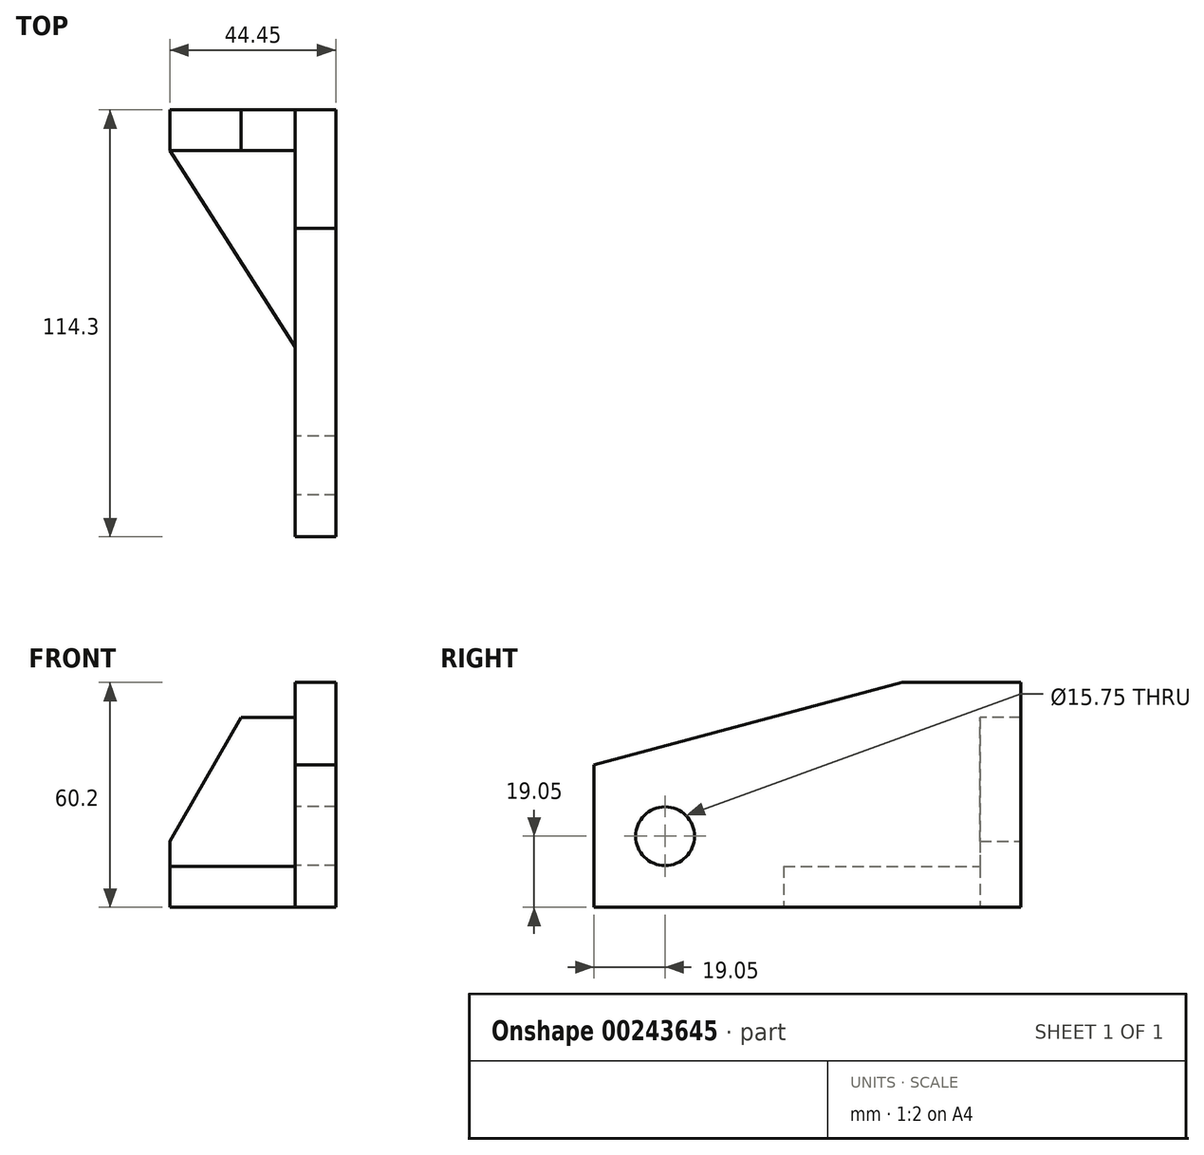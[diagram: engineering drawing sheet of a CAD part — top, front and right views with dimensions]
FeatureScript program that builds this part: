
annotation { "Feature Type Name" : "Feature", "Feature Type Description" : "" }
export const myFeature = defineFeature(function(context is Context, id is Id, definition is map)
    precondition{}
    {
        {
            var Q0;
            Q0=qCreatedBy(makeId("Top.planeOp"),FACE);
            var sketch = newSketch(context, id + "F0", { "sketchPlane" : qUnion([Q0])});
            skLineSegment(sketch, "E0", {"start": v(-20.72, 21.7) * mm, "end": v(12.81, 21.7) * mm});
            skLineSegment(sketch, "E1", {"start": v(12.81, -30.88) * mm, "end": v(12.81, 21.7) * mm});
            skLineSegment(sketch, "E2", {"start": v(-20.72, 21.7) * mm, "end": v(12.81, -30.88) * mm});
            skLineSegment(sketch, "E3", {"start": v(-20.72, 21.7) * mm, "end": v(-20.72, 32.62) * mm});
            skLineSegment(sketch, "E4", {"start": v(-20.72, 32.62) * mm, "end": v(12.81, 32.62) * mm});
            skLineSegment(sketch, "E5", {"start": v(12.81, 32.62) * mm, "end": v(12.81, 21.7) * mm});
            skLineSegment(sketch, "E6", {"start": v(12.81, 32.62) * mm, "end": v(23.73, 32.62) * mm});
            skLineSegment(sketch, "E7", {"start": v(23.73, 32.62) * mm, "end": v(23.73, -81.68) * mm});
            skLineSegment(sketch, "E8", {"start": v(23.73, -81.68) * mm, "end": v(12.81, -81.68) * mm});
            skLineSegment(sketch, "E9", {"start": v(12.81, -81.68) * mm, "end": v(12.81, -30.88) * mm});
            skSolve(sketch);
        }
        {
            var Q0;
            Q0=makeQuery(id+"F0.imprint","IMPRINT",FACE,{"disambiguationData":[TD([[makeQuery(id+"F0.imprint","IMPRINT",EDGE,{"derivedFrom":sQuery(id+"F0.wireOp",EDGE,"E0")}),-1.0]])]});
            extrude(context, id + "F1", {"entities" : qUnion([Q0]), "depth" : 10.92 * mm});
        }
        {
            var Q0;
            Q0=makeQuery(id+"F0.imprint","IMPRINT",FACE,{"disambiguationData":[TD([[makeQuery(id+"F0.imprint","IMPRINT",EDGE,{"derivedFrom":sQuery(id+"F0.wireOp",EDGE,"E1")}),-1.0]])]});
            extrude(context, id + "F2", {"entities" : qUnion([Q0]), "operationType" : NewBodyOperationType.ADD, "depth" : 60.2 * mm});
        }
        {
            var Q0;
            Q0=makeQuery(id+"F0.imprint","IMPRINT",FACE,{"disambiguationData":[TD([[makeQuery(id+"F0.imprint","IMPRINT",EDGE,{"derivedFrom":sQuery(id+"F0.wireOp",EDGE,"E0")}),1.0]])]});
            extrude(context, id + "F3", {"entities" : qUnion([Q0]), "operationType" : NewBodyOperationType.ADD, "depth" : 50.8 * mm});
        }
        {
            var Q0;
            Q0=makeQuery(id+"F3.opExtrude","CAP_EDGE",EDGE,{"disambiguationData":[OSD([sQuery(id+"F0.wireOp",EDGE,"E3")])],"isStart":false});
            chamfer(context, id + "F4", {"entities" : qUnion([Q0]), "chamferType" : ChamferType.OFFSET_ANGLE, "width" : 33.14 * mm, "oppositeDirection" : false, "angle" : 30 * degree, "tangentPropagation" : true});
        }
        {
            var Q0;
            Q0=makeQuery(id+"F2.opExtrude","CAP_EDGE",EDGE,{"disambiguationData":[OSD([sQuery(id+"F0.wireOp",EDGE,"E8")])],"isStart":false});
            chamfer(context, id + "F5", {"entities" : qUnion([Q0]), "chamferType" : ChamferType.TWO_OFFSETS, "width1" : 22.1 * mm, "oppositeDirection" : false, "width2" : 82.55 * mm, "tangentPropagation" : true});
        }
        {
            var Q0;
            Q0=makeQuery(id+"F2.opExtrude","SWEPT_FACE",FACE,{"disambiguationData":[OSD([sQuery(id+"F0.wireOp",EDGE,"E9")])]});
            var sketch = newSketch(context, id + "F6", { "sketchPlane" : qUnion([Q0])});
            skCircle(sketch, "E10", {"center": v(62.63, 19.05) * mm, "radius": 7.87 * mm});
            skSolve(sketch);
        }
        {
            var Q0;
            Q0=sQuery(id+"F6.wireOp",VERTEX,"E10.center");
            var Q1;
            Q1=makeQuery(id+"F1.opExtrude","SWEPT_BODY",BODY,{"disambiguationData":[OSD([sQuery(id+"F0.wireOp",EDGE,"E0"),sQuery(id+"F0.wireOp",EDGE,"E1"),sQuery(id+"F0.wireOp",EDGE,"E2")])]});
            hole(context, id + "F7", {"style" : HoleStyle.SIMPLE, "endStyle" : HoleEndStyle.THROUGH, "holeDiameter" : 15.75 * mm, "tappedDepth" : 12.7 * mm, "tapClearance" : 3, "locations" : qUnion([Q0]), "scope" : qUnion([Q1])});
        }
    });
